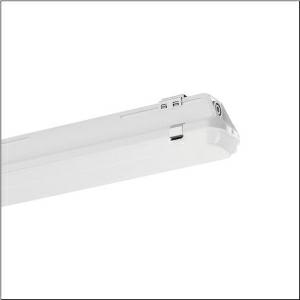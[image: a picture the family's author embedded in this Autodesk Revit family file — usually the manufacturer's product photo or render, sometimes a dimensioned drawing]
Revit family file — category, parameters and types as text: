
# Revit family: monsun_r__21_emergency_51fb107p437c3g_98c5
name_source: partatom
category: Lighting Fixtures
units: mm (PartAtom-declared; Revit-internal decimal feet)

## family parameters
Cut with Voids When Loaded = No
Host = Face
Light Source = No
Part Type = Normal
Room Calculation Point = No
Round Connector Dimension = Use Diameter
Shared = No

## types (1)
- --- (1 x LED, 910 lm, 7.1 W, 4000K)
    Apparent Load = 7 VA
    CIE Flux Codes = 47 77 93 94 100
    Color Rendering = 80
    Color Temperature = 4000K
    Default Elevation = 1800 mm
    Description = Monsun® 21 emergency, damp-proof luminaire, chain hanger, primary optical cover: enclosure, of PMMA, light emission: direct distribution, primary light characteristic: symmetric, installation type: suspended mounting, surface-mounted, horizontal mounting, vertical mounting, LED, rated luminous flux: 3.860lm, luminous efficacy: 175lm/W, light colour: 840, colour temperature: 4000K, control gear: ON/OFF, with terminal, 4-pole, max. 2.5mm², mains connection: 220..240V, AC, 50/60Hz, rated input power: 26W, control gear: single battery element, battery: LiFePO4, 9Ah, housing, of glass-fibre reinforced polyester, uncoated, bright grey, incl. chain hanger, length: 1.590mm, width: 90mm, height: 88mm, clip for enclosure, of stainless steel (V2A), ceiling mounting element, of stainless steel (V2A), chain hanger, of stainless steel (V2A), protection rating (complete): IP66, insulation class (complete): insulation class I (protective earthing), certification: CE, UKCA, protection symbol: D, impact resistance: IK04, permissible operating ambient temperature: +5..+25°C, standard: EN 50419, EN 60598-2-1, EN 60598-2-22, corresponds to IFS (International Featured Standards) requirements for safety and quality in the food industry, for indoor or canopied outdoor use, no direct snow, no direct sun, no direct rain, LABS conformity tested according to VDMA 24364:2018-05, contact your sales advisor before using the luminaires in applications with unclear chemical exposure, large temperature fluctuations or condensation-forming humidity, packaging unit: 1 piece
    Height = 89 mm
    Lamp = 1 x LED
    Lamp Light Flux = 910 lm
    Lamp Power = 7.1 W
    Lamp count = 1
    Length = 1590 mm
    Luminous efficacy = 128 lm/W
    Manufacturer = Siteco
    ModVariant = No
    Model = 51FB107P437C3G
    Mounting Place = Ceiling
    Mounting Type = Surface mounted
    Number of Poles = 1
    OnlyDefault = Yes
    Power Factor = 1
    Product Name = Monsun® 21 emergency
    Product group = damp-proof luminaire
    ProductGroupID = 301
    Protection Class = Protection class I
    Protection Degree = IP 66
    RLX_Detail_Level = 1
    RLX_Emergency_Light_Flux = 0 lm
    RLX_Emergency_Type = 0
    RLX_Emergency_Type_DB = No
    RlxData = <blob elided: 88981 chars, md5=26d00a82>
    Socket = socket
    Standby Power = 0 W
    System Light Flux = 910 lm
    System Power = 7 W
    Type Comments = : emergency light operation: 3 h
    Type Image = l_1319656.jpg
    URL = http://relux.com
    VarID = @adj_051775
    Voltage = 0 V
    Weight = 0.00 kg
    Width = 90 mm

## geometry (parser evidence)
native form markers: Blend x4, Sweep x14
no freeform markers — native parametric forms only
